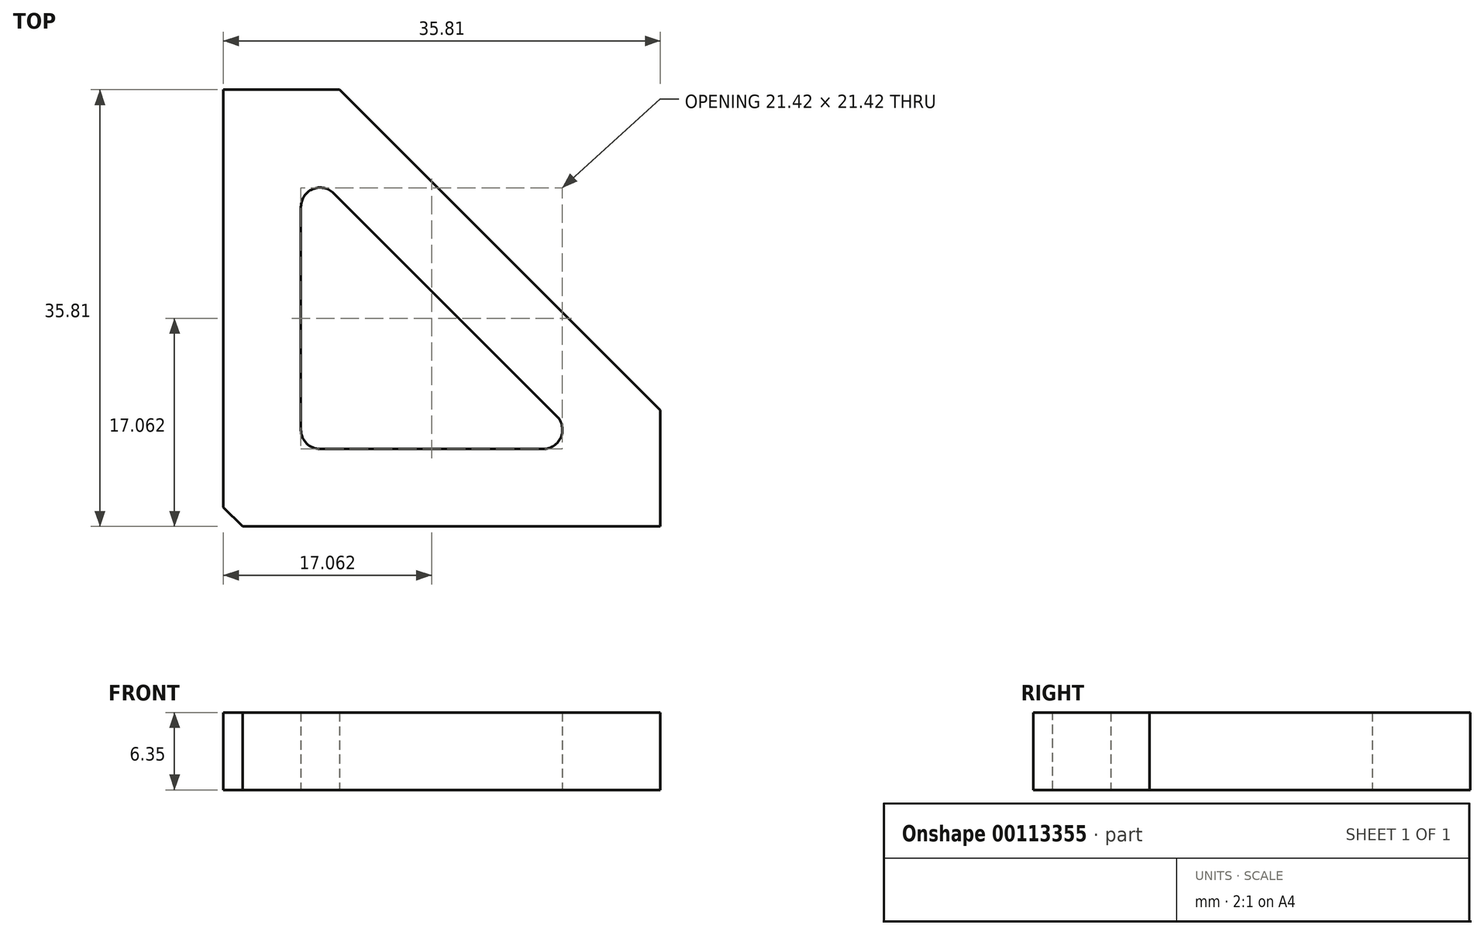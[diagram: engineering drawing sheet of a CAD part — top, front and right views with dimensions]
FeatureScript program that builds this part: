
annotation { "Feature Type Name" : "Feature", "Feature Type Description" : "" }
export const myFeature = defineFeature(function(context is Context, id is Id, definition is map)
    precondition{}
    {
        {
            var Q0;
            Q0=qCreatedBy(makeId("Top.planeOp"),FACE);
            var sketch = newSketch(context, id + "F0", { "sketchPlane" : qUnion([Q0])});
            skLineSegment(sketch, "E0", {"start": v(0, 35.81) * mm, "end": v(0, 0) * mm});
            skLineSegment(sketch, "E1", {"start": v(0, 0) * mm, "end": v(35.81, 0) * mm});
            skLineSegment(sketch, "E2", {"start": v(35.81, 0) * mm, "end": v(35.81, 9.53) * mm});
            skLineSegment(sketch, "E3", {"start": v(35.81, 9.53) * mm, "end": v(9.53, 35.81) * mm});
            skLineSegment(sketch, "E4", {"start": v(9.53, 35.81) * mm, "end": v(0, 35.81) * mm});
            skLineSegment(sketch, "E5", {"start": v(6.35, 26.2) * mm, "end": v(6.35, 7.92) * mm});
            skLineSegment(sketch, "E6", {"start": v(7.92, 6.35) * mm, "end": v(26.2, 6.35) * mm});
            skLineSegment(sketch, "E7", {"start": v(27.32, 9.04) * mm, "end": v(9.04, 27.32) * mm});
            skPoint(sketch, "E8.visualSharp", {"position": v(6.35, 30) * mm});
            skArc(sketch, "E8.filletArc", {"start": v(9.04, 27.32) * mm, "mid": v(7.32, 27.66) * mm, "end": v(6.35, 26.2) * mm});
            skPoint(sketch, "E9.visualSharp", {"position": v(6.35, 6.35) * mm});
            skArc(sketch, "E9.filletArc", {"start": v(6.35, 7.92) * mm, "mid": v(6.81, 6.81) * mm, "end": v(7.92, 6.35) * mm});
            skPoint(sketch, "E10.visualSharp", {"position": v(30, 6.35) * mm});
            skArc(sketch, "E10.filletArc", {"start": v(26.2, 6.35) * mm, "mid": v(27.66, 7.32) * mm, "end": v(27.32, 9.04) * mm});
            skSolve(sketch);
        }
        {
            var Q0;
            Q0=makeQuery(id+"F0.imprint","IMPRINT",FACE,{"disambiguationData":[TD([[makeQuery(id+"F0.imprint","IMPRINT",EDGE,{"derivedFrom":sQuery(id+"F0.wireOp",EDGE,"E0")}),1.0]])]});
            extrude(context, id + "F1", {"entities" : qUnion([Q0]), "depth" : 6.35 * mm, "offsetDistance" : 25.4 * mm});
        }
        {
            var Q0;
            Q0=makeQuery(id+"F1.opExtrude","SWEPT_EDGE",EDGE,{"disambiguationData":[OSD([sQuery(id+"F0.wireOp",EDGE,"E0"),sQuery(id+"F0.wireOp",EDGE,"E1")])]});
            chamfer(context, id + "F2", {"entities" : qUnion([Q0]), "width" : 1.57 * mm, "tangentPropagation" : true});
        }
    });
